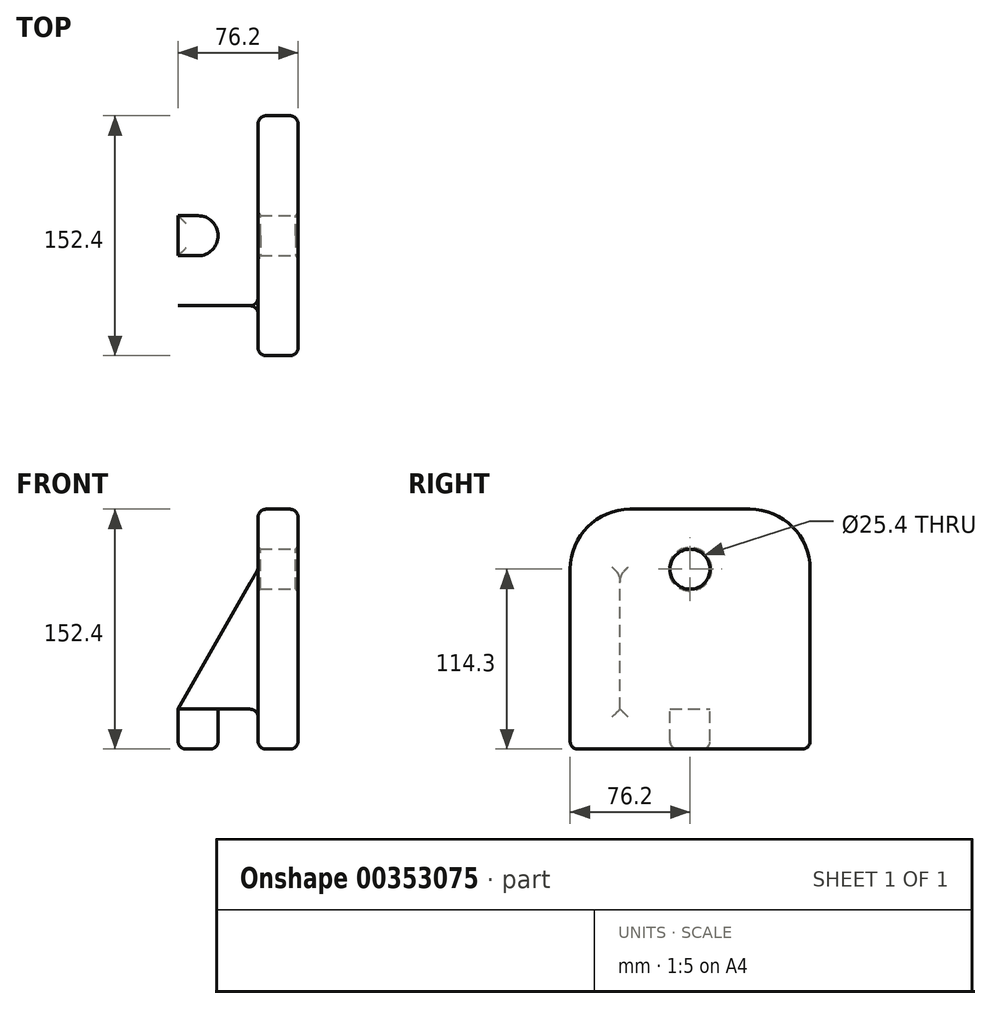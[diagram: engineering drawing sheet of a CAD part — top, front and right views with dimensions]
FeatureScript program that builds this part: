
annotation { "Feature Type Name" : "Feature", "Feature Type Description" : "" }
export const myFeature = defineFeature(function(context is Context, id is Id, definition is map)
    precondition{}
    {
        {
            var Q0;
            Q0=qCreatedBy(makeId("Front.planeOp"),FACE);
            var sketch = newSketch(context, id + "F0", { "sketchPlane" : qUnion([Q0])});
            skLineSegment(sketch, "E0", {"start": v(0, 0) * mm, "end": v(0, 152.4) * mm});
            skLineSegment(sketch, "E1", {"start": v(0, 152.4) * mm, "end": v(-25.4, 152.4) * mm});
            skLineSegment(sketch, "E2", {"start": v(-25.4, 152.4) * mm, "end": v(-25.4, 25.4) * mm});
            skLineSegment(sketch, "E3", {"start": v(-25.4, 25.4) * mm, "end": v(-76.2, 25.4) * mm});
            skLineSegment(sketch, "E4", {"start": v(-76.2, 25.4) * mm, "end": v(-76.2, 0) * mm});
            skLineSegment(sketch, "E5", {"start": v(-76.2, 0) * mm, "end": v(0, 0) * mm});
            skSolve(sketch);
        }
        {
            var Q0;
            Q0=makeQuery(id+"F0.imprint","IMPRINT",FACE,{"disambiguationData":[TD([[makeQuery(id+"F0.imprint","IMPRINT",EDGE,{"derivedFrom":sQuery(id+"F0.wireOp",EDGE,"E0")}),1.0]])]});
            extrude(context, id + "F1", {"entities" : qUnion([Q0]), "endBound" : BoundingType.SYMMETRIC, "depth" : 152.4 * mm});
        }
        {
            var Q0;
            Q0=makeQuery(id+"F1.opExtrude","SWEPT_FACE",FACE,{"disambiguationData":[OSD([sQuery(id+"F0.wireOp",EDGE,"E0")])]});
            var sketch = newSketch(context, id + "F2", { "sketchPlane" : qUnion([Q0])});
            skCircle(sketch, "E6", {"center": v(0, 114.3) * mm, "radius": 12.7 * mm});
            skSolve(sketch);
        }
        {
            var Q0;
            Q0=makeQuery(id+"F2.imprint","IMPRINT",FACE,{"disambiguationData":[TD([[makeQuery(id+"F2.imprint","IMPRINT",EDGE,{"derivedFrom":sQuery(id+"F2.wireOp",EDGE,"E6")}),1.0]])]});
            extrude(context, id + "F3", {"entities" : qUnion([Q0]), "operationType" : NewBodyOperationType.REMOVE, "endBound" : BoundingType.THROUGH_ALL, "oppositeDirection" : true, "depth" : 25.4 * mm});
        }
        {
            var Q0;
            Q0=makeQuery(id+"F1.opExtrude","SWEPT_FACE",FACE,{"disambiguationData":[OSD([sQuery(id+"F0.wireOp",EDGE,"E3")])]});
            var sketch = newSketch(context, id + "F4", { "sketchPlane" : qUnion([Q0])});
            skPoint(sketch, "E7.endSnap0", {"position": v(-76.2, 0) * mm});
            skPoint(sketch, "E7.end.orphan", {"position": v(-63.5, 0) * mm});
            skPoint(sketch, "E7.start.orphan", {"position": v(-76.2, 0) * mm});
            skArc(sketch, "E8", {"start": v(-63.5, 12.7) * mm, "mid": v(-50.8, 0) * mm, "end": v(-63.5, -12.7) * mm});
            skLineSegment(sketch, "E9", {"start": v(-63.5, 12.7) * mm, "end": v(-76.2, 12.7) * mm});
            skLineSegment(sketch, "E10", {"start": v(-63.5, -12.7) * mm, "end": v(-76.2, -12.7) * mm});
            skSolve(sketch);
        }
        {
            var Q0;
            Q0=makeQuery(id+"F4.imprint","IMPRINT",FACE,{"disambiguationData":[TD([[makeQuery(id+"F4.imprint","IMPRINT",EDGE,{"derivedFrom":sQuery(id+"F4.wireOp",EDGE,"E8")}),-1.0]])]});
            extrude(context, id + "F5", {"entities" : qUnion([Q0]), "operationType" : NewBodyOperationType.REMOVE, "endBound" : BoundingType.THROUGH_ALL, "oppositeDirection" : true, "depth" : 25.4 * mm});
        }
        {
            var Q0;
            Q0=makeQuery(id+"F1.opExtrude","CAP_EDGE",EDGE,{"disambiguationData":[OSD([sQuery(id+"F0.wireOp",EDGE,"E1")])],"isStart":true});
            fillet(context, id + "F6", {"entities" : qUnion([Q0]), "radius" : 38.1 * mm, "tangentPropagation" : true, "allowEdgeOverflow" : false});
        }
        {
            var Q0;
            Q0=makeQuery(id+"F1.opExtrude","CAP_EDGE",EDGE,{"disambiguationData":[OSD([sQuery(id+"F0.wireOp",EDGE,"E1")])],"isStart":false});
            fillet(context, id + "F7", {"entities" : qUnion([Q0]), "radius" : 38.1 * mm, "tangentPropagation" : true, "allowEdgeOverflow" : false});
        }
        {
            var Q0;
            Q0=qCreatedBy(makeId("Front.planeOp"),FACE);
            cPlane(context, id + "F8", {"entities" : qUnion([Q0]), "cplaneType" : CPlaneType.OFFSET, "offset" : 44.45 * mm, "width" : 152.4 * mm, "height" : 152.4 * mm});
        }
        {
            var Q0;
            Q0=qCreatedBy(id+"F8.planeOp",FACE);
            var sketch = newSketch(context, id + "F9", { "sketchPlane" : qUnion([Q0])});
            skLineSegment(sketch, "E11.0", {"start": v(-25.4, 25.4) * mm, "end": v(-76.2, 25.4) * mm});
            skLineSegment(sketch, "E12.0", {"start": v(-25.4, 114.3) * mm, "end": v(-25.4, 25.4) * mm});
            skLineSegment(sketch, "E13", {"start": v(-76.2, 25.4) * mm, "end": v(-25.4, 114.3) * mm});
            skLineSegment(sketch, "E14", {"start": v(-76.2, 25.4) * mm, "end": v(-25.4, 25.4) * mm});
            skSolve(sketch);
        }
        {
            var Q0;
            Q0=makeQuery(id+"F9.imprint","IMPRINT",FACE,{"disambiguationData":[TD([[makeQuery(id+"F9.imprint","IMPRINT",EDGE,{"derivedFrom":sQuery(id+"F9.wireOp",EDGE,"E12.0")}),-1.0]])]});
            extrude(context, id + "F10", {"entities" : qUnion([Q0]), "operationType" : NewBodyOperationType.ADD, "endBound" : BoundingType.SYMMETRIC, "depth" : 1 / 50.8 * mm});
        }
        {
            var Q0;
            Q0=makeQuery(id+"F3.boolean.opBoolean","COPY",FACE,{"derivedFrom":makeQuery(id+"F3.opExtrude","SWEPT_FACE",FACE,{"disambiguationData":[OSD([sQuery(id+"F2.wireOp",EDGE,"E6")])]})});
            chamfer(context, id + "F11", {"entities" : qUnion([Q0]), "width" : 1.52 * mm, "tangentPropagation" : true});
        }
        {
            var Q0;
            {var subQ0=makeQuery(id+"F1.opExtrude","SWEPT_FACE",FACE,{"disambiguationData":[OSD([sQuery(id+"F0.wireOp",EDGE,"E2")])]});Q0=makeQuery(id+"F11.opChamfer","BLEND_EDGE",EDGE,{"blendedFrom":[makeQuery(id+"F3.boolean.opBoolean","INTERSECT",EDGE,{"derivedFrom":[subQ0,makeQuery(id+"F3.opExtrude","SWEPT_FACE",FACE,{"disambiguationData":[OSD([sQuery(id+"F2.wireOp",EDGE,"E6")])]})]}),subQ0],"blendedInto":[subQ0]});}
            chamfer(context, id + "F12", {"entities" : qUnion([Q0]), "width" : 1.52 * mm, "tangentPropagation" : true});
        }
        {
            var Q0;
            Q0=makeQuery(id+"F1.opExtrude","SWEPT_FACE",FACE,{"disambiguationData":[OSD([sQuery(id+"F0.wireOp",EDGE,"E2")])]});
            var Q1;
            Q1=makeQuery(id+"F1.opExtrude","SWEPT_FACE",FACE,{"disambiguationData":[OSD([sQuery(id+"F0.wireOp",EDGE,"E1")])]});
            var Q2;
            Q2=makeQuery(id+"F6.opFillet","BLEND_FACE",FACE,{"disambiguationData":[OSD([sQuery(id+"F0.wireOp",EDGE,"E1")])]});
            var Q3;
            Q3=makeQuery(id+"F7.opFillet","BLEND_FACE",FACE,{"disambiguationData":[OSD([sQuery(id+"F0.wireOp",EDGE,"E1")])]});
            var Q4;
            Q4=makeQuery(id+"F1.opExtrude","SWEPT_FACE",FACE,{"disambiguationData":[OSD([sQuery(id+"F0.wireOp",EDGE,"E0")])]});
            var Q5;
            Q5=makeQuery(id+"F1.opExtrude","SWEPT_FACE",FACE,{"disambiguationData":[OSD([sQuery(id+"F0.wireOp",EDGE,"E5")])]});
            fillet(context, id + "F13", {"entities" : qUnion([Q0, Q1, Q2, Q3, Q4, Q5]), "radius" : 5.08 * mm, "tangentPropagation" : true, "allowEdgeOverflow" : false});
        }
    });
